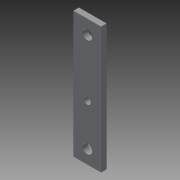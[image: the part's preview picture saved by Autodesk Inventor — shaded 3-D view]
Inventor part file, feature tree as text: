
AUTODESK INVENTOR PART (.ipt)
format: ipt  version: 2015 (Build 190159000, 159)  size: 113,664 bytes
history: native  units: mm
features: extrude x1, sketch x1
ambient origin geometry x8: Origin, YZ Plane, XZ Plane, XY Plane, X Axis, Y Axis, Z Axis, Center Point
bodies: Solid1 (feature_tree)
feature tree (2):
  extrude  "Extrusion1"  Depth=4.0mm
  sketch  "Sketch1"  dims[d0=21.0mm d1=23.5mm d2=10.5mm d3=11.75mm d5=23.5mm d6=5.0mm d7=23.5mm d9=70.5mm d40=21.625mm d41=70.5mm d42=91.5mm d43=10.0mm d44=10.0mm d45=7.0mm d46=10.0mm d47=10.0mm d48=90.0deg d50=7.0mm d51=10.0mm d52=10.0mm d53=7.0mm d54=10.0mm d55=10.0mm d56=7.0mm d60=30.0mm d61=30.0mm d62=5.0mm d63=5.0mm d64=14.0mm d65=20.0mm d66=4.0mm d67=0.0mm]
